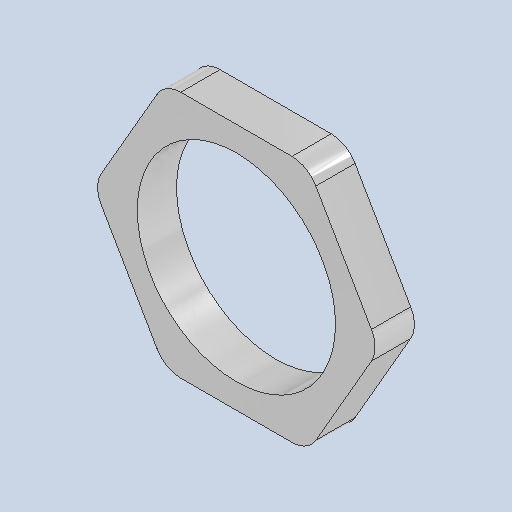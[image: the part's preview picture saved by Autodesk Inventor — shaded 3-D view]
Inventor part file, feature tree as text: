
AUTODESK INVENTOR PART (.ipt)
format: ipt  version: 2024.2 (Build 282272000, 272)  size: 121,856 bytes
history: native  units: mm
features: extrude x1, fillet x1, sketch x1
ambient origin geometry x8: Origin, YZ Plane, XZ Plane, XY Plane, X Axis, Y Axis, Z Axis, Center Point
bodies: Solid1 (feature_tree)
feature tree (3):
  extrude  "Extrusion1"  Depth=2.0mm
  fillet  "Fillet1"  Radius=2.85mm
  sketch  "Sketch1"  dims[d0=18.0mm d1=14.4mm d2=2.85mm d3=0.0mm d4=2.0mm]
